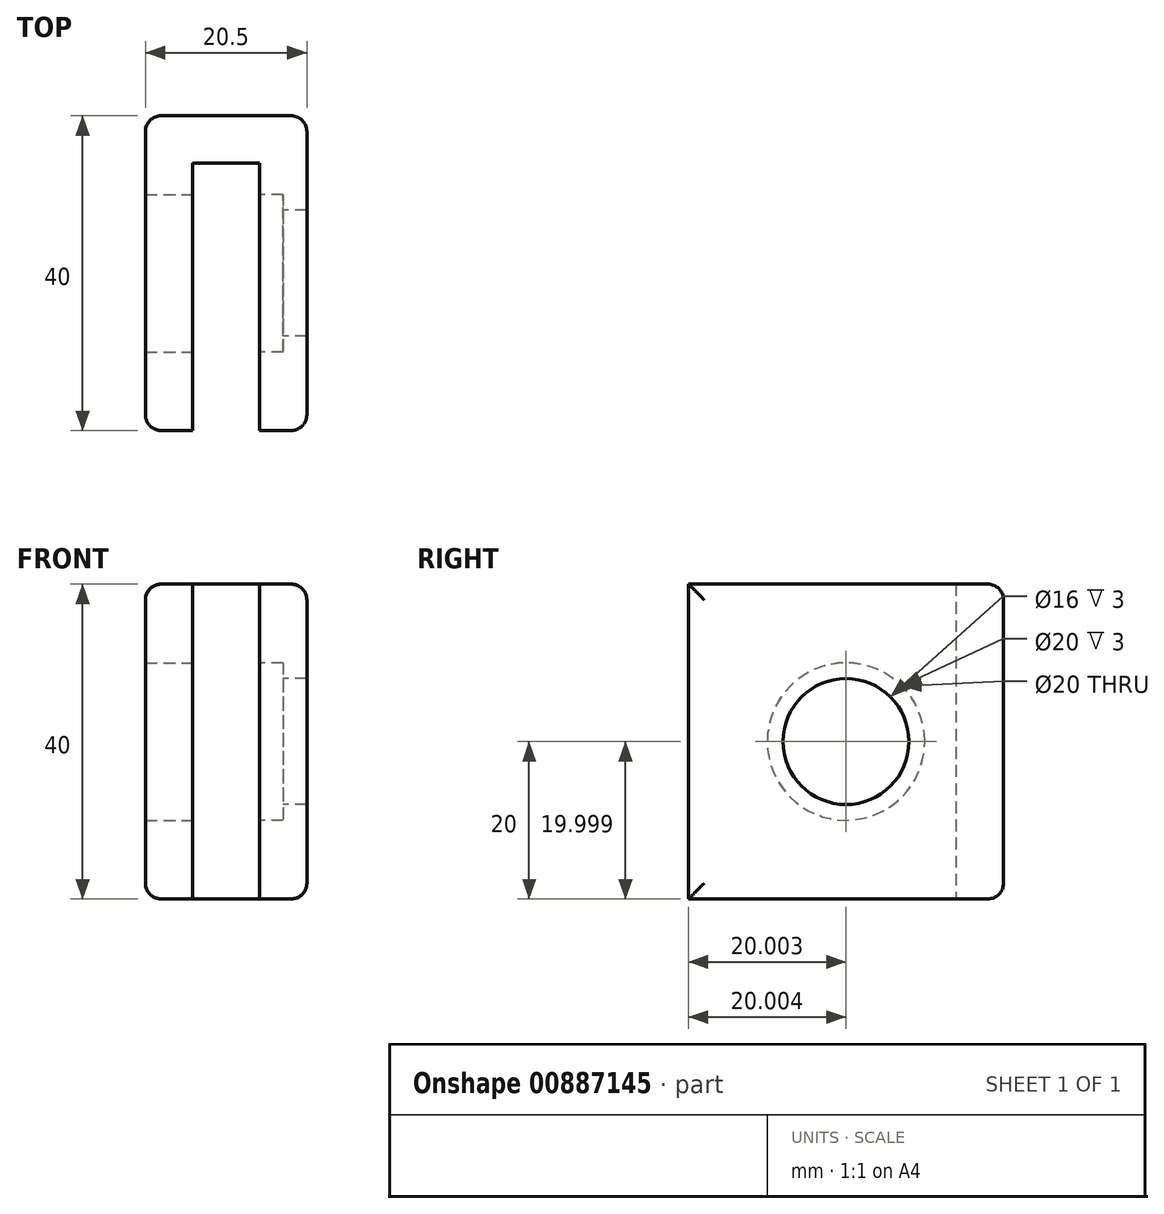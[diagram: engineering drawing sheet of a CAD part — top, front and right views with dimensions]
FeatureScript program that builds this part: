
annotation { "Feature Type Name" : "Feature", "Feature Type Description" : "" }
export const myFeature = defineFeature(function(context is Context, id is Id, definition is map)
    precondition{}
    {
        {
            var Q0;
            Q0=qCreatedBy(makeId("Top.planeOp"),FACE);
            var sketch = newSketch(context, id + "F0", { "sketchPlane" : qUnion([Q0])});
            skLineSegment(sketch, "E0.bottom", {"start": v(-8.5, 18.48) * mm, "end": v(0, 18.48) * mm});
            skLineSegment(sketch, "E0.top", {"start": v(-8.5, 12.48) * mm, "end": v(0, 12.48) * mm});
            skLineSegment(sketch, "E0.left", {"start": v(-8.5, 18.48) * mm, "end": v(-8.5, 12.48) * mm});
            skLineSegment(sketch, "E0.right", {"start": v(0, 18.48) * mm, "end": v(0, 12.48) * mm});
            skLineSegment(sketch, "E1.bottom", {"start": v(-14.5, 18.48) * mm, "end": v(-8.5, 18.48) * mm});
            skLineSegment(sketch, "E1.top", {"start": v(-14.5, -21.52) * mm, "end": v(-8.5, -21.52) * mm});
            skLineSegment(sketch, "E1.left", {"start": v(-14.5, 18.48) * mm, "end": v(-14.5, -21.52) * mm});
            skLineSegment(sketch, "E1.right", {"start": v(-8.5, 18.48) * mm, "end": v(-8.5, -21.52) * mm});
            skLineSegment(sketch, "E2.bottom", {"start": v(0, 18.48) * mm, "end": v(6, 18.48) * mm});
            skLineSegment(sketch, "E2.top", {"start": v(0, -21.52) * mm, "end": v(6, -21.52) * mm});
            skLineSegment(sketch, "E2.left", {"start": v(0, 18.48) * mm, "end": v(0, -21.52) * mm});
            skLineSegment(sketch, "E2.right", {"start": v(6, 18.48) * mm, "end": v(6, -21.52) * mm});
            skSolve(sketch);
        }
        {
            var Q0;
            {var subQ1=sQuery(id+"F0.wireOp",EDGE,"E1.bottom");Q0=makeQuery(id+"F0.imprint","IMPRINT",FACE,{"disambiguationData":[TD([[makeQuery(id+"F0.imprint","IMPRINT",EDGE,{"derivedFrom":subQ1}),-1.0]])]});}
            var Q1;
            {var subQ0=sQuery(id+"F0.wireOp",EDGE,"E0.bottom");Q1=makeQuery(id+"F0.imprint","IMPRINT",FACE,{"disambiguationData":[TD([[makeQuery(id+"F0.imprint","IMPRINT",EDGE,{"derivedFrom":subQ0}),-1.0]])]});}
            var Q2;
            {var subQ3=sQuery(id+"F0.wireOp",EDGE,"E2.bottom");Q2=makeQuery(id+"F0.imprint","IMPRINT",FACE,{"disambiguationData":[TD([[makeQuery(id+"F0.imprint","IMPRINT",EDGE,{"derivedFrom":subQ3}),-1.0]])]});}
            var Q3;
            Q3=sQuery(id+"F0.wireOp",EDGE,"E2.left");
            var Q4;
            Q4=sQuery(id+"F0.wireOp",EDGE,"E0.left");
            var Q5;
            Q5=sQuery(id+"F0.wireOp",EDGE,"E1.bottom");
            var Q6;
            Q6=sQuery(id+"F0.wireOp",EDGE,"E1.left");
            var Q7;
            Q7=sQuery(id+"F0.wireOp",EDGE,"E1.right");
            var Q8;
            Q8=sQuery(id+"F0.wireOp",EDGE,"E1.top");
            extrude(context, id + "F1", {"entities" : qUnion([Q0, Q1, Q2]), "surfaceEntities" : qUnion([Q3, Q4, Q5, Q6, Q7, Q8]), "depth" : 40 * mm, "offsetDistance" : 25 * mm});
        }
        {
            var Q0;
            Q0=qCreatedBy(makeId("Right.planeOp"),FACE);
            var sketch = newSketch(context, id + "F2", { "sketchPlane" : qUnion([Q0])});
            skPoint(sketch, "E3", {"position": v(-1.52, 20) * mm});
            skLineSegment(sketch, "E4", {"start": v(-1.52, 40) * mm, "end": v(-1.52, 0) * mm, "construction": true});
            skLineSegment(sketch, "E5", {"start": v(-21.56, 20) * mm, "end": v(18.48, 20) * mm, "construction": true});
            skSolve(sketch);
        }
        {
            var Q0;
            Q0=sQuery(id+"F2.wireOp",VERTEX,"E3");
            var Q1;
            Q1=makeQuery(id+"F1.opExtrude","SWEPT_BODY",BODY,{"disambiguationData":[OSD([sQuery(id+"F0.wireOp",EDGE,"E0.bottom"),sQuery(id+"F0.wireOp",EDGE,"E0.top"),sQuery(id+"F0.wireOp",EDGE,"E1.bottom"),sQuery(id+"F0.wireOp",EDGE,"E1.top"),sQuery(id+"F0.wireOp",EDGE,"E1.left"),sQuery(id+"F0.wireOp",EDGE,"E1.right"),sQuery(id+"F0.wireOp",EDGE,"E2.bottom"),sQuery(id+"F0.wireOp",EDGE,"E2.top"),sQuery(id+"F0.wireOp",EDGE,"E2.left"),sQuery(id+"F0.wireOp",EDGE,"E2.right")])]});
            hole(context, id + "F3", {"style" : HoleStyle.C_BORE, "endStyle" : HoleEndStyle.THROUGH, "oppositeDirection" : true, "standardTappedOrClearance" : lookupTablePath({ "fit" : "Standard", "standard" : "ISO", "size" : "M3", "type" : "Clearance" }), "standardBlindInLast" : lookupTablePath({ "fit" : "Standard", "standard" : "ISO", "size" : "M3", "type" : "Clearance" }), "holeDiameter" : 16 * mm, "cBoreDiameter" : 20 * mm, "cBoreDepth" : 3 * mm, "majorDiameter" : 5 * mm, "isTappedThrough" : true, "tappedDepth" : 12 * mm, "tapClearance" : 3, "locations" : qUnion([Q0]), "scope" : qUnion([Q1])});
        }
        {
            var Q0;
            Q0=qCreatedBy(makeId("Right.planeOp"),FACE);
            cPlane(context, id + "F4", {"entities" : qUnion([Q0]), "cplaneType" : CPlaneType.OFFSET, "offset" : 8.5 * mm, "oppositeDirection" : true, "width" : 150 * mm, "height" : 150 * mm});
        }
        {
            var Q0;
            Q0=qCreatedBy(id+"F4.planeOp",FACE);
            var sketch = newSketch(context, id + "F5", { "sketchPlane" : qUnion([Q0])});
            skPoint(sketch, "E6", {"position": v(-1.52, 20) * mm});
            skSolve(sketch);
        }
        {
            var Q0;
            Q0=sQuery(id+"F5.wireOp",VERTEX,"E6");
            var Q1;
            Q1=makeQuery(id+"F1.opExtrude","SWEPT_BODY",BODY,{"disambiguationData":[OSD([sQuery(id+"F0.wireOp",EDGE,"E0.bottom"),sQuery(id+"F0.wireOp",EDGE,"E0.top"),sQuery(id+"F0.wireOp",EDGE,"E1.bottom"),sQuery(id+"F0.wireOp",EDGE,"E1.top"),sQuery(id+"F0.wireOp",EDGE,"E1.left"),sQuery(id+"F0.wireOp",EDGE,"E1.right"),sQuery(id+"F0.wireOp",EDGE,"E2.bottom"),sQuery(id+"F0.wireOp",EDGE,"E2.top"),sQuery(id+"F0.wireOp",EDGE,"E2.left"),sQuery(id+"F0.wireOp",EDGE,"E2.right")])]});
            hole(context, id + "F6", {"style" : HoleStyle.SIMPLE, "endStyle" : HoleEndStyle.THROUGH, "holeDiameter" : 20 * mm, "majorDiameter" : 5 * mm, "isTappedThrough" : true, "tappedDepth" : 12 * mm, "tapClearance" : 3, "locations" : qUnion([Q0]), "scope" : qUnion([Q1])});
        }
        {
            var Q0;
            Q0=makeQuery(id+"F1.opExtrude","SWEPT_EDGE",EDGE,{"disambiguationData":[OSD([sQuery(id+"F0.wireOp",EDGE,"E1.top"),sQuery(id+"F0.wireOp",EDGE,"E1.left")])]});
            var Q1;
            Q1=makeQuery(id+"F1.opExtrude","CAP_EDGE",EDGE,{"disambiguationData":[OSD([sQuery(id+"F0.wireOp",EDGE,"E1.left")])],"isStart":false});
            var Q2;
            Q2=makeQuery(id+"F1.opExtrude","CAP_EDGE",EDGE,{"disambiguationData":[OSD([sQuery(id+"F0.wireOp",EDGE,"E1.left")])],"isStart":true});
            var Q3;
            Q3=makeQuery(id+"F1.opExtrude","CAP_EDGE",EDGE,{"disambiguationData":[OSD([sQuery(id+"F0.wireOp",EDGE,"E2.right")])],"isStart":true});
            var Q4;
            Q4=makeQuery(id+"F1.opExtrude","CAP_EDGE",EDGE,{"disambiguationData":[OSD([sQuery(id+"F0.wireOp",EDGE,"E2.right")])],"isStart":false});
            var Q5;
            Q5=makeQuery(id+"F1.opExtrude","SWEPT_EDGE",EDGE,{"disambiguationData":[OSD([sQuery(id+"F0.wireOp",EDGE,"E2.top"),sQuery(id+"F0.wireOp",EDGE,"E2.right")])]});
            var Q6;
            Q6=makeQuery(id+"F1.opExtrude","SWEPT_FACE",FACE,{"disambiguationData":[OSD([sQuery(id+"F0.wireOp",EDGE,"E0.bottom"),sQuery(id+"F0.wireOp",EDGE,"E1.bottom"),sQuery(id+"F0.wireOp",EDGE,"E2.bottom")])]});
            fillet(context, id + "F7", {"entities" : qUnion([Q0, Q1, Q2, Q3, Q4, Q5, Q6]), "radius" : 2 * mm, "tangentPropagation" : true, "defaultsChanged" : false, "vertexSettings" : [], "allowEdgeOverflow" : false});
        }
    });
